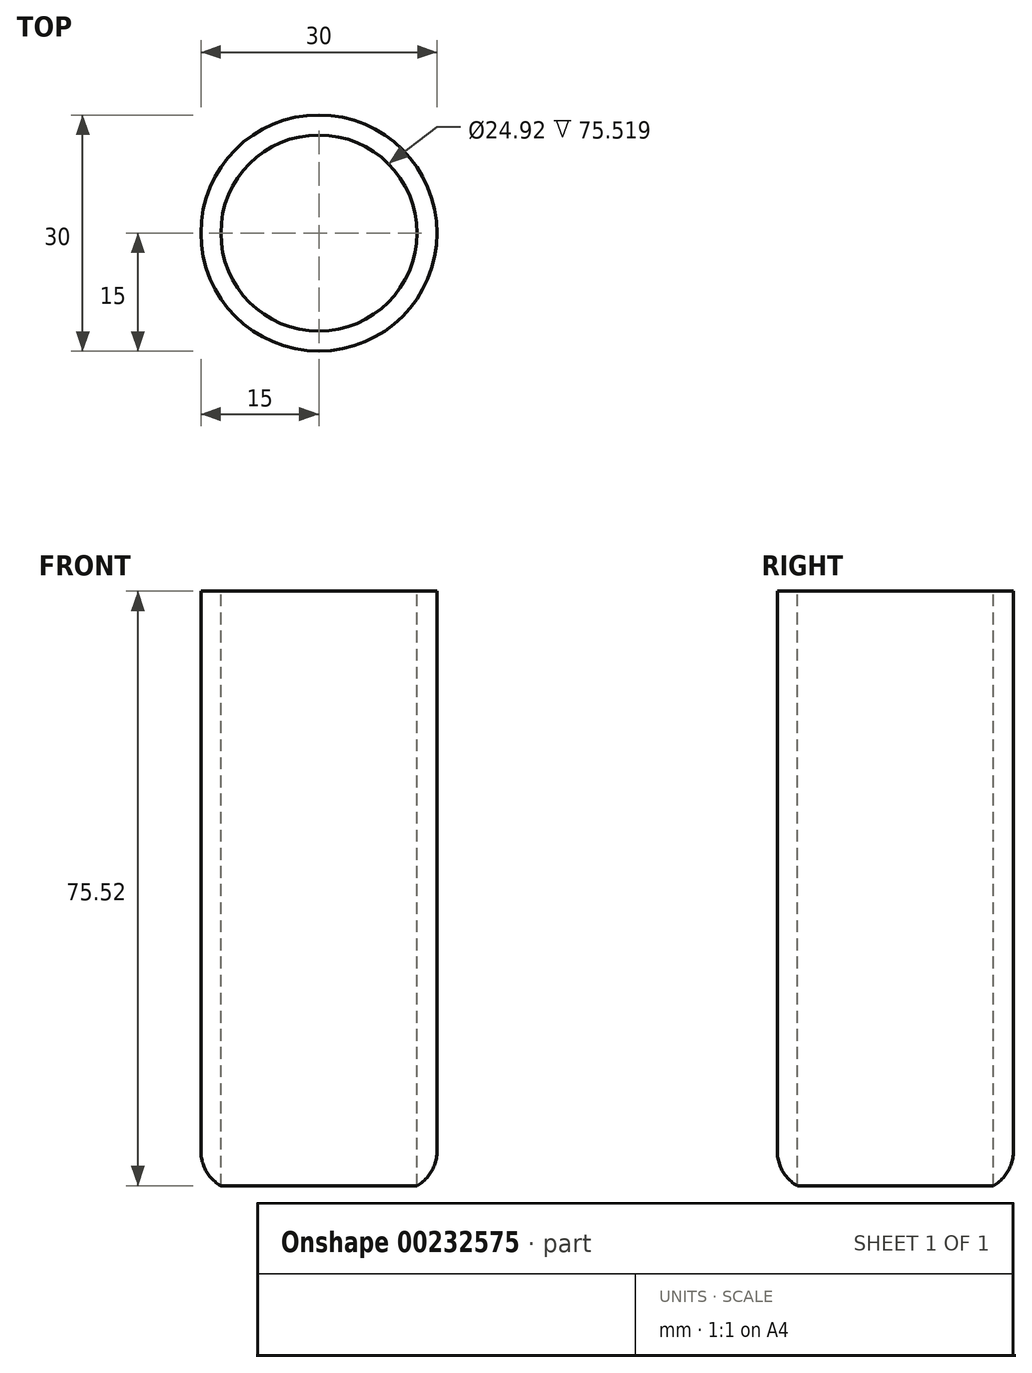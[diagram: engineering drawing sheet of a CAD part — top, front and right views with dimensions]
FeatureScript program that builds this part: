
annotation { "Feature Type Name" : "Feature", "Feature Type Description" : "" }
export const myFeature = defineFeature(function(context is Context, id is Id, definition is map)
    precondition{}
    {
        {
            var Q0;
            Q0=qCreatedBy(makeId("Top.planeOp"),FACE);
            var sketch = newSketch(context, id + "F0", { "sketchPlane" : qUnion([Q0])});
            skCircle(sketch, "E0", {"center": v(0, 0) * mm, "radius": 15 * mm});
            skSolve(sketch);
        }
        {
            var Q0;
            Q0=makeQuery(id+"F0.imprint","IMPRINT",FACE,{"disambiguationData":[TD([[makeQuery(id+"F0.imprint","IMPRINT",EDGE,{"derivedFrom":sQuery(id+"F0.wireOp",EDGE,"E0")}),1.0]])]});
            extrude(context, id + "F1", {"entities" : qUnion([Q0]), "depth" : 76.2 * mm});
        }
        {
            var Q0;
            Q0=makeQuery(id+"F1.opExtrude","CAP_EDGE",EDGE,{"disambiguationData":[OSD([sQuery(id+"F0.wireOp",EDGE,"E0")])],"isStart":true});
            fillet(context, id + "F2", {"entities" : qUnion([Q0]), "radius" : 5.08 * mm, "tangentPropagation" : true, "allowEdgeOverflow" : false});
        }
        {
            var Q0;
            Q0=makeQuery(id+"F1.opExtrude","CAP_FACE",FACE,{"disambiguationData":[OSD([sQuery(id+"F0.wireOp",EDGE,"E0")])],"isStart":false});
            var sketch = newSketch(context, id + "F3", { "sketchPlane" : qUnion([Q0])});
            skCircle(sketch, "E1", {"center": v(0, 0) * mm, "radius": 12.46 * mm});
            skSolve(sketch);
        }
        {
            var Q0;
            Q0=makeQuery(id+"F3.imprint","IMPRINT",FACE,{"disambiguationData":[TD([[makeQuery(id+"F3.imprint","IMPRINT",EDGE,{"derivedFrom":sQuery(id+"F3.wireOp",EDGE,"E1")}),1.0]])]});
            extrude(context, id + "F4", {"entities" : qUnion([Q0]), "operationType" : NewBodyOperationType.REMOVE, "endBound" : BoundingType.THROUGH_ALL, "oppositeDirection" : true, "depth" : 25.4 * mm});
        }
    });
